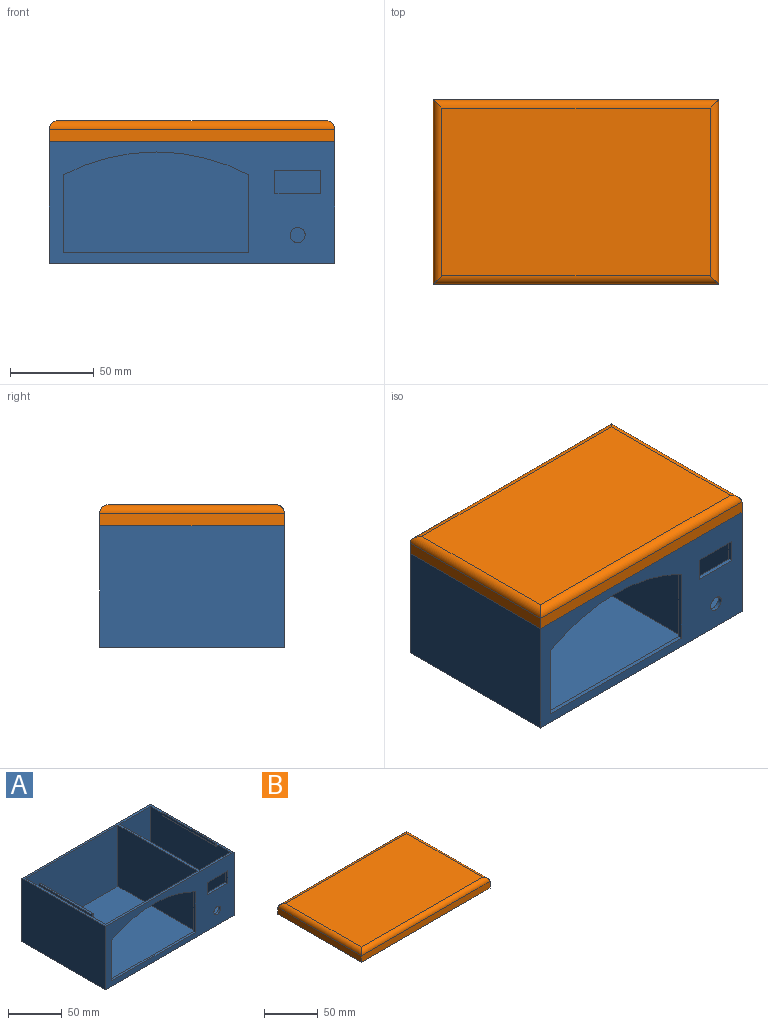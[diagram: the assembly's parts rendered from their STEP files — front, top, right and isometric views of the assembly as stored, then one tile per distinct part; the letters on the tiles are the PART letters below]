
ASSEMBLY  parts=2 mates=1
PART A: 56 faces, bbox 170x110x75 mm
  f0: plane 105x70mm, normal (1,0,0), area 7175mm2, adj f4,f10,f12,f13,f45,f46,f49
  f1: plane 70x40.75mm, normal (0,1,0), area 2293.9mm2, adj f3,f4,f11,f15,f20,f21,f22,f23
  f2: plane 70x40.75mm, normal (0,-1,0), area 2852.5mm2, adj f3,f4,f11,f15
  f3: plane 105x40.75mm, normal (0,0,1), area 4278.8mm2, adj f1,f2,f11,f15
  f4: plane 170x110mm, normal (0,0,1), area 1637.5mm2, adj f0,f1,f2,f5,f6,f7,f8,f10
  f5: plane 170x72.5mm, normal (0,-1,0), area 5709.6mm2, adj f4,f6,f8,f9,f16,f17,f18,f19
  f6: plane 110x72.5mm, normal (1,0,0), area 7911.4mm2, adj f4,f5,f7,f9,f25
  f7: plane 170x72.5mm, normal (0,1,0), area 12325mm2, adj f4,f6,f8,f9
  f8: plane 110x72.5mm, normal (-1,0,0), area 7975mm2, adj f4,f5,f7,f9
  f9: plane 170x110mm, normal (0,0,-1), area 18700mm2, adj f5,f6,f7,f8
  f10: plane 121.75x70mm, normal (0,1,0), area 2348.7mm2, adj f0,f4,f13,f14,f16,f17,f18,f19
  f11: plane 105x70mm, normal (-1,0,0), area 7111.4mm2, adj f1,f2,f3,f4,f25,f50,f51,f55
  f12: plane 121.75x70mm, normal (0,-1,0), area 8522.5mm2, adj f0,f4,f13,f14
  f13: plane 121.75x105mm, normal (0,0,1), area 12783.7mm2, adj f0,f10,f12,f14
  f14: plane 105x70mm, normal (-1,0,0), area 7350mm2, adj f4,f10,f12,f13
  f15: plane 105x70mm, normal (1,0,0), area 7350mm2, adj f1,f2,f3,f4
  f16: cylinder r=119mm len=110.64mm, axis (0,-1,0), area 287.7mm2, adj f5,f10,f17,f19
  f17: plane 46.6x2.5mm, normal (1,0,0), area 116.5mm2, adj f5,f10,f16,f18
  f18: plane 110.64x2.5mm, normal (0,0,1), area 276.6mm2, adj f5,f10,f17,f19
  f19: plane 46.6x2.5mm, normal (-1,0,0), area 116.5mm2, adj f5,f10,f16,f18
  f20: plane 14x2.5mm, normal (1,0,0), area 35mm2, adj f1,f5,f21,f22
  f21: plane 27x4.5mm, normal (0,0,-1), area 93.5mm2, adj f1,f5,f20,f23,f26,f28,f29,f30
  f22: plane 27x2.5mm, normal (0,0,1), area 67.5mm2, adj f1,f5,f20,f23
  f23: plane 14x2.5mm, normal (-1,0,0), area 35mm2, adj f1,f5,f21,f22
  f24: cylinder r=4.5mm len=9mm, axis (0,-1,0), area 70.7mm2, adj f1,f5
  f25: cylinder r=4.5mm len=9mm, axis (1,0,0), area 70.7mm2, adj f6,f11
  f26: plane 4.5x2mm, normal (-1,0,0), area 9mm2, adj f1,f21,f27,f29
  f27: plane 6.5x2mm, normal (0,0,1), area 13mm2, adj f1,f26,f28,f29
  f28: plane 4.5x2mm, normal (1,0,0), area 9mm2, adj f1,f21,f27,f29
  f29: plane 6.5x4.5mm, normal (0,1,0), area 29.3mm2, adj f21,f26,f27,f28
  f30: plane 4.5x2mm, normal (1,0,0), area 9mm2, adj f1,f21,f32,f33
  f31: plane 4.5x2mm, normal (-1,0,0), area 9mm2, adj f1,f21,f32,f33
  f32: plane 6.5x2mm, normal (0,0,1), area 13mm2, adj f1,f30,f31,f33
  f33: plane 6.5x4.5mm, normal (0,1,0), area 29.2mm2, adj f21,f30,f31,f32
  f34: plane 6.5x2mm, normal (0,0,1), area 13mm2, adj f1,f35,f37,f38
  f35: plane 4.5x2mm, normal (1,0,0), area 9mm2, adj f1,f34,f36,f38
  f36: plane 6.5x2mm, normal (0,0,-1), area 13mm2, adj f1,f35,f37,f38
  f37: plane 4.5x2mm, normal (-1,0,0), area 9mm2, adj f1,f34,f36,f38
  f38: plane 6.5x4.5mm, normal (0,1,0), area 29.2mm2, adj f34,f35,f36,f37
  f39: plane 4.5x2mm, normal (-1,0,0), area 9mm2, adj f1,f40,f42,f43
  f40: plane 6.5x2mm, normal (0,0,1), area 13mm2, adj f1,f39,f41,f43
  f41: plane 4.5x2mm, normal (1,0,0), area 9mm2, adj f1,f40,f42,f43
  f42: plane 6.5x2mm, normal (0,0,-1), area 13mm2, adj f1,f39,f41,f43
  f43: plane 6.5x4.5mm, normal (0,1,0), area 29.2mm2, adj f39,f40,f41,f42
  f44: plane 70x2.5mm, normal (-1,0,0), area 175mm2, adj f4,f45,f46,f47
  f45: plane 5x2mm, normal (0,-1,0), area 8mm2, adj f0,f44,f47,f48,f49
  f46: plane 5x2mm, normal (0,1,0), area 8mm2, adj f0,f44,f47,f48,f49
  f47: plane 70x2mm, normal (0,0,1), area 140mm2, adj f44,f45,f46,f48
  f48: plane 70x3mm, normal (1,0,0), area 210mm2, adj f45,f46,f47,f49
  f49: plane 70x2mm, normal (0.71,0,-0.71), area 198mm2, adj f0,f45,f46,f48
  f50: plane 5x2mm, normal (0,1,0), area 8mm2, adj f11,f52,f53,f54,f55
  f51: plane 5x2mm, normal (0,-1,0), area 8mm2, adj f11,f52,f53,f54,f55
  f52: plane 70x2mm, normal (0,0,1), area 140mm2, adj f50,f51,f53,f54
  f53: plane 70x3mm, normal (-1,0,0), area 210mm2, adj f50,f51,f52,f55
  f54: plane 70x2.5mm, normal (1,0,0), area 175mm2, adj f4,f50,f51,f52
  f55: plane 70x2mm, normal (-0.71,0,-0.71), area 198mm2, adj f11,f50,f51,f53
PART B: 35 faces, bbox 170x110x12.5 mm
  f0: plane 165x10mm, normal (0,-1,0), area 1554mm2, adj f1,f2,f3,f9,f18,f19,f21,f22
  f1: plane 165x105mm, normal (0,0,-1), area 16749mm2, adj f0,f2,f9,f10,f11,f12,f14,f15
  f2: plane 105x10mm, normal (1,0,0), area 954mm2, adj f0,f1,f3,f10,f14,f16,f20,f22
  f3: plane 170x110mm, normal (0,0,-1), area 1375mm2, adj f0,f2,f4,f5,f6,f7,f9,f10
  f4: plane 110x7.5mm, normal (1,0,0), area 825mm2, adj f3,f5,f7,f23
  f5: plane 170x7.5mm, normal (0,1,0), area 1275mm2, adj f3,f4,f6,f24
  f6: plane 110x7.5mm, normal (-1,0,0), area 825mm2, adj f3,f5,f7,f26
  f7: plane 170x7.5mm, normal (0,-1,0), area 1275mm2, adj f3,f4,f6,f25
  f8: plane 160x100mm, normal (0,0,1), area 16000mm2, adj f23,f24,f25,f26
  f9: plane 105x10mm, normal (-1,0,0), area 954mm2, adj f0,f1,f3,f10,f11,f13,f17,f19
  f10: plane 165x10mm, normal (0,1,0), area 1554mm2, adj f1,f2,f3,f9,f12,f13,f15,f16
  f11: plane 12x4mm, normal (0,1,0), area 48mm2, adj f1,f9,f12,f13
  f12: plane 12x4mm, normal (-1,0,0), area 48mm2, adj f1,f10,f11,f13
  f13: plane 12x12mm, normal (0,0,-1), area 136.9mm2, adj f9,f10,f11,f12,f34
  f14: plane 12x4mm, normal (0,1,0), area 48mm2, adj f1,f2,f15,f16
  f15: plane 12x4mm, normal (1,0,0), area 48mm2, adj f1,f10,f14,f16
  f16: plane 12x12mm, normal (0,0,-1), area 136.9mm2, adj f2,f10,f14,f15,f32
  f17: plane 12x4mm, normal (0,-1,0), area 48mm2, adj f1,f9,f18,f19
  f18: plane 12x4mm, normal (-1,0,0), area 48mm2, adj f0,f1,f17,f19
  f19: plane 12x12mm, normal (0,0,-1), area 136.9mm2, adj f0,f9,f17,f18,f30
  f20: plane 12x4mm, normal (0,-1,0), area 48mm2, adj f1,f2,f21,f22
  f21: plane 12x4mm, normal (1,0,0), area 48mm2, adj f0,f1,f20,f22
  f22: plane 12x12mm, normal (0,0,-1), area 136.9mm2, adj f0,f2,f20,f21,f28
  f23: cylinder r=5mm len=110mm, axis (0,1,0), area 835.4mm2, adj f4,f8,f24,f25
  f24: cylinder r=5mm len=170mm, axis (-1,0,0), area 1306.6mm2, adj f5,f8,f23,f26
  f25: cylinder r=5mm len=170mm, axis (1,0,0), area 1306.6mm2, adj f7,f8,f23,f26
  f26: cylinder r=5mm len=110mm, axis (0,-1,0), area 835.4mm2, adj f6,f8,f24,f25
  f27: cone r=0mm half-angle=59deg, axis (0,0,-1), area 8.2mm2, adj f28
  f28: cylinder r=1.5mm len=3mm, axis (0,0,-1), area 28.3mm2, adj f22,f27
  f29: cone r=0mm half-angle=59deg, axis (0,0,-1), area 8.2mm2, adj f30
  f30: cylinder r=1.5mm len=3mm, axis (0,0,-1), area 28.3mm2, adj f19,f29
  f31: cone r=0mm half-angle=59deg, axis (0,0,-1), area 8.2mm2, adj f32
  f32: cylinder r=1.5mm len=3mm, axis (0,0,-1), area 28.3mm2, adj f16,f31
  f33: cone r=0mm half-angle=59deg, axis (0,0,-1), area 8.2mm2, adj f34
  f34: cylinder r=1.5mm len=3mm, axis (0,0,-1), area 28.3mm2, adj f13,f33
PLACE A t=(-25.37,-0.57,-13.88)mm fixed
PLACE B t=(-25.37,-0.57,-3.88)mm
MATE fastened B.f3 <-> A.f4  axis (0,0,1) through (-110.37,-55.57,56.12)mm
